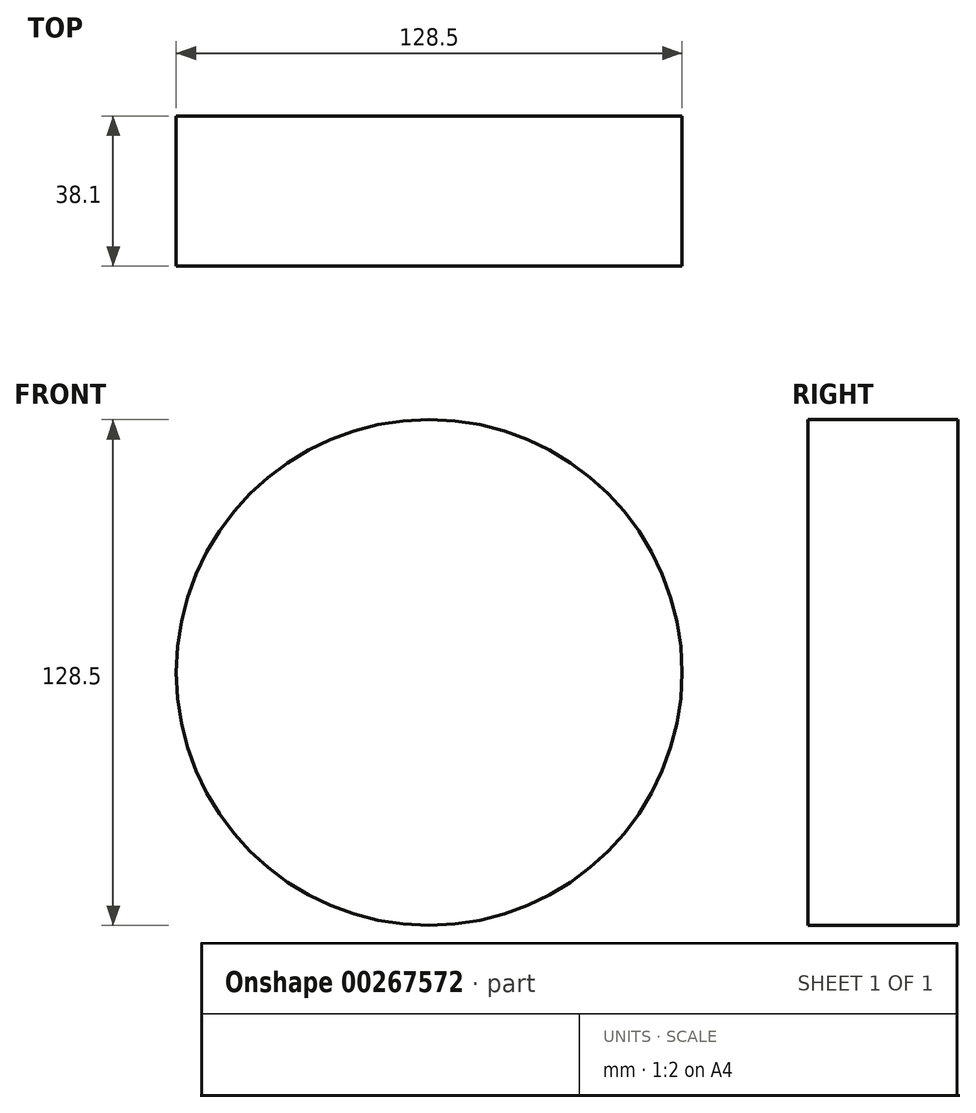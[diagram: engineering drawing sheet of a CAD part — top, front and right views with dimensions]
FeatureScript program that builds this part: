
annotation { "Feature Type Name" : "Feature", "Feature Type Description" : "" }
export const myFeature = defineFeature(function(context is Context, id is Id, definition is map)
    precondition{}
    {
        {
            var Q0;
            Q0=qCreatedBy(makeId("Front.planeOp"),FACE);
            var sketch = newSketch(context, id + "F0", { "sketchPlane" : qUnion([Q0])});
            skCircle(sketch, "E0", {"center": v(0, 0) * mm, "radius": 64.25 * mm});
            skSolve(sketch);
        }
        {
            var Q0;
            Q0 = qSketchRegion(id + "F0", true);
            extrude(context, id + "F1", {"entities" : qUnion([Q0]), "depth" : 38.1 * mm});
        }
    });
